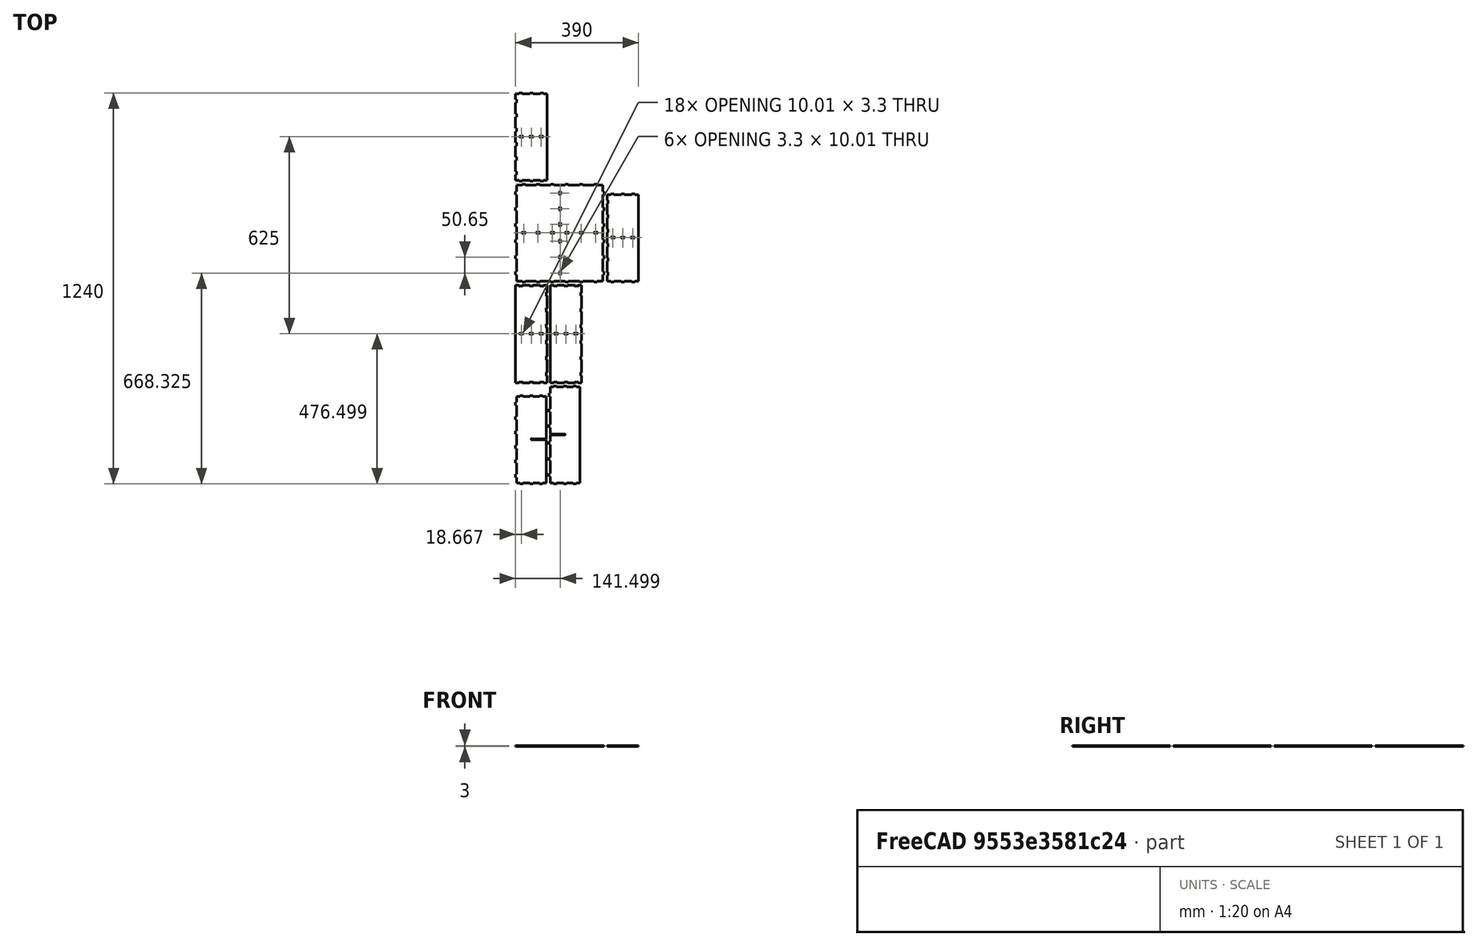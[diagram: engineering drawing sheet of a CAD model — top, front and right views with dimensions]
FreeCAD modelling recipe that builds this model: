
FCSTD DOCUMENT  (FreeCAD 0.19R14555 (Git shallow))
Label: 10x4sections
License: All rights reserved
LicenseURL: http://en.wikipedia.org/wiki/All_rights_reserved
objects: Part::Feature×7, Part::Part2DObjectPython×7
note: 14 computed .brp shape members not serialized (recipe doc carries the construction recipe); baked Part::Feature solids carry a one-line shape summary decoded from their .brp

FEATURE [Part::Feature] test
  Placement = pos=(50,140,33) rot=(-1,0,0;1.5708rad)
  shape: bbox 97 x 280 x 3 mm, 68 faces (baked)
FEATURE [Part::Feature] test001
  Placement = pos=(157,155,30) rot=(0,0,1;0rad)
  shape: bbox 97 x 310 x 3 mm, 60 faces (baked)
FEATURE [Part::Feature] test002
  Placement = pos=(50,475,170) rot=(0,-1,0;3.14159rad)
  shape: bbox 100 x 310 x 3 mm, 102 faces (baked)
FEATURE [Part::Feature] test003
  Placement = pos=(160,475,-107) rot=(0,-1,0;3.14159rad)
  shape: bbox 100 x 310 x 3 mm, 102 faces (baked)
FEATURE [Part::Feature] test004
  Placement = pos=(140,795,-17) rot=(0,1,0;1.5708rad)
  shape: bbox 280 x 310 x 3 mm, 198 faces (baked)
FEATURE [Part::Feature] test005
  Placement = pos=(340,780,-122) rot=(-1,0,0;1.5708rad)
  shape: bbox 100 x 280 x 3 mm, 90 faces (baked)
FEATURE [Part::Feature] test006
  Placement = pos=(50,1100,185) rot=(-1,0,0;1.5708rad)
  shape: bbox 100 x 280 x 3 mm, 90 faces (baked)
FEATURE [Part::Part2DObjectPython] Shape2DView  # Draft 2D object (typed FeaturePython)
  Base = -> test
  FuseArch = false
  HiddenLines = false
  InPlace = true
  Projection = (0,0,1)
  ProjectionMode = 0
  SegmentLength = 0.05
  Tessellation = false
  VisibleOnly = false
FEATURE [Part::Part2DObjectPython] Shape2DView001  # Draft 2D object (typed FeaturePython)
  Base = -> test001
  FuseArch = false
  HiddenLines = false
  InPlace = true
  Projection = (0,0,1)
  ProjectionMode = 0
  SegmentLength = 0.05
  Tessellation = false
  VisibleOnly = false
FEATURE [Part::Part2DObjectPython] Shape2DView002  # Draft 2D object (typed FeaturePython)
  Base = -> test002
  FuseArch = false
  HiddenLines = false
  InPlace = true
  Projection = (0,0,1)
  ProjectionMode = 0
  SegmentLength = 0.05
  Tessellation = false
  VisibleOnly = false
FEATURE [Part::Part2DObjectPython] Shape2DView003  # Draft 2D object (typed FeaturePython)
  Base = -> test003
  FuseArch = false
  HiddenLines = false
  InPlace = true
  Projection = (0,0,1)
  ProjectionMode = 0
  SegmentLength = 0.05
  Tessellation = false
  VisibleOnly = false
FEATURE [Part::Part2DObjectPython] Shape2DView004  # Draft 2D object (typed FeaturePython)
  Base = -> test004
  FuseArch = false
  HiddenLines = false
  InPlace = true
  Projection = (0,0,1)
  ProjectionMode = 0
  SegmentLength = 0.05
  Tessellation = false
  VisibleOnly = false
FEATURE [Part::Part2DObjectPython] Shape2DView005  # Draft 2D object (typed FeaturePython)
  Base = -> test005
  FuseArch = false
  HiddenLines = false
  InPlace = true
  Projection = (0,0,1)
  ProjectionMode = 0
  SegmentLength = 0.05
  Tessellation = false
  VisibleOnly = false
FEATURE [Part::Part2DObjectPython] Shape2DView006  # Draft 2D object (typed FeaturePython)
  Base = -> test006
  FuseArch = false
  HiddenLines = false
  InPlace = true
  Projection = (0,0,1)
  ProjectionMode = 0
  SegmentLength = 0.05
  Tessellation = false
  VisibleOnly = false
